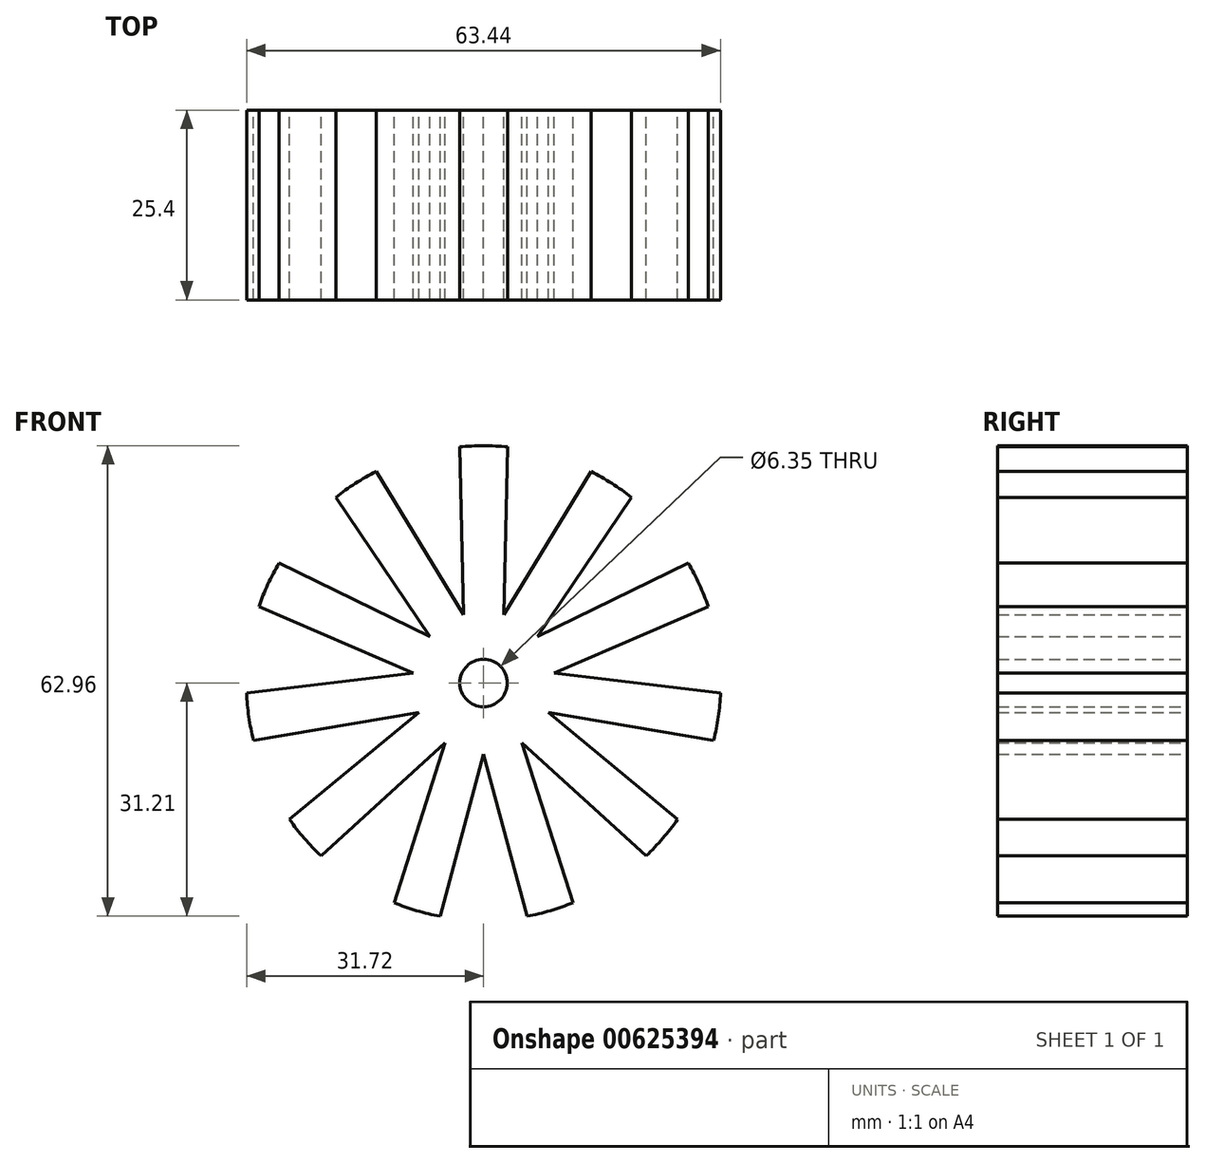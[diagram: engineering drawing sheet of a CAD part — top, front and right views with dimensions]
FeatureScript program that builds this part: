
annotation { "Feature Type Name" : "Feature", "Feature Type Description" : "" }
export const myFeature = defineFeature(function(context is Context, id is Id, definition is map)
    precondition{}
    {
        {
            var Q0;
            Q0=qCreatedBy(makeId("Front.planeOp"),FACE);
            var sketch = newSketch(context, id + "F0", { "sketchPlane" : qUnion([Q0])});
            skCircle(sketch, "E0", {"center": v(0, 0) * mm, "radius": 31.75 * mm});
            skLineSegment(sketch, "E1", {"start": v(-5.81, -31.21) * mm, "end": v(0, -9.52) * mm});
            skLineSegment(sketch, "E2", {"start": v(0, -9.53) * mm, "end": v(5.81, -31.21) * mm});
            skLineSegment(sketch, "E3", {"start": v(0, -31.75) * mm, "end": v(0, 0) * mm});
            skLineSegment(sketch, "E4.1.0", {"start": v(5.15, -8.01) * mm, "end": v(21.76, -23.12) * mm});
            skLineSegment(sketch, "E4.1.1", {"start": v(11.99, -29.4) * mm, "end": v(5.15, -8.01) * mm});
            skLineSegment(sketch, "E4.2.0", {"start": v(8.66, -3.96) * mm, "end": v(30.8, -7.68) * mm});
            skLineSegment(sketch, "E4.2.1", {"start": v(25.98, -18.25) * mm, "end": v(8.66, -3.96) * mm});
            skLineSegment(sketch, "E4.3.0", {"start": v(9.43, 1.36) * mm, "end": v(30.07, 10.2) * mm});
            skLineSegment(sketch, "E4.3.1", {"start": v(31.72, -1.31) * mm, "end": v(9.43, 1.36) * mm});
            skLineSegment(sketch, "E4.4.0", {"start": v(7.2, 6.24) * mm, "end": v(19.78, 24.83) * mm});
            skLineSegment(sketch, "E4.4.1", {"start": v(27.4, 16.05) * mm, "end": v(7.2, 6.24) * mm});
            skLineSegment(sketch, "E4.5.0", {"start": v(2.68, 9.14) * mm, "end": v(3.22, 31.59) * mm});
            skLineSegment(sketch, "E4.5.1", {"start": v(14.37, 28.31) * mm, "end": v(2.68, 9.14) * mm});
            skLineSegment(sketch, "E4.6.0", {"start": v(-2.68, 9.14) * mm, "end": v(-14.37, 28.31) * mm});
            skLineSegment(sketch, "E4.6.1", {"start": v(-3.22, 31.59) * mm, "end": v(-2.68, 9.14) * mm});
            skLineSegment(sketch, "E4.7.0", {"start": v(-7.2, 6.24) * mm, "end": v(-27.4, 16.05) * mm});
            skLineSegment(sketch, "E4.7.1", {"start": v(-19.78, 24.83) * mm, "end": v(-7.2, 6.24) * mm});
            skLineSegment(sketch, "E4.8.0", {"start": v(-9.43, 1.36) * mm, "end": v(-31.72, -1.31) * mm});
            skLineSegment(sketch, "E4.8.1", {"start": v(-30.07, 10.2) * mm, "end": v(-9.43, 1.36) * mm});
            skLineSegment(sketch, "E4.9.0", {"start": v(-8.66, -3.96) * mm, "end": v(-25.98, -18.25) * mm});
            skLineSegment(sketch, "E4.9.1", {"start": v(-30.8, -7.68) * mm, "end": v(-8.66, -3.96) * mm});
            skLineSegment(sketch, "E5.0.10.0", {"start": v(-5.15, -8.01) * mm, "end": v(-11.99, -29.4) * mm});
            skLineSegment(sketch, "E5.3.10.0", {"start": v(-21.76, -23.12) * mm, "end": v(-5.15, -8.01) * mm});
            skCircle(sketch, "E6", {"center": v(0, 0) * mm, "radius": 9.53 * mm});
            skLineSegment(sketch, "E7.bottom", {"start": v(3.18, 3.18) * mm, "end": v(-3.18, 3.18) * mm, "construction": true});
            skLineSegment(sketch, "E7.top", {"start": v(3.18, -3.18) * mm, "end": v(-3.17, -3.18) * mm, "construction": true});
            skLineSegment(sketch, "E7.left", {"start": v(3.18, 3.18) * mm, "end": v(3.18, -3.18) * mm, "construction": true});
            skLineSegment(sketch, "E7.right", {"start": v(-3.18, 3.17) * mm, "end": v(-3.18, -3.18) * mm, "construction": true});
            skCircle(sketch, "E8", {"center": v(0, 0) * mm, "radius": 3.17 * mm});
            skSolve(sketch);
        }
        {
            var Q0;
            {var subQ0=sQuery(id+"F0.wireOp",EDGE,"E4.7.0");Q0=makeQuery(id+"F0.imprint","IMPRINT",FACE,{"disambiguationData":[TD([[makeQuery(id+"F0.imprint","IMPRINT",EDGE,{"derivedFrom":subQ0}),1.0]])]});}
            var Q1;
            {var subQ0=sQuery(id+"F0.wireOp",EDGE,"E4.6.0");Q1=makeQuery(id+"F0.imprint","IMPRINT",FACE,{"disambiguationData":[TD([[makeQuery(id+"F0.imprint","IMPRINT",EDGE,{"derivedFrom":subQ0}),1.0]])]});}
            var Q2;
            {var subQ0=sQuery(id+"F0.wireOp",EDGE,"E6");var subQ8=makeQuery(id+"F0.imprint","INTERSECT",VERTEX,{"derivedFrom":[sQuery(id+"F0.wireOp",EDGE,"E4.3.0"),sQuery(id+"F0.wireOp",EDGE,"E4.3.1"),subQ0]});Q2=makeQuery(id+"F0.imprint","IMPRINT",FACE,{"disambiguationData":[TD([[makeQuery(id+"F0.imprint","IMPRINT",EDGE,{"disambiguationData":[TD([[subQ8,-1.0]])],"derivedFrom":subQ0}),1.0]])]});}
            var Q3;
            {var subQ0=sQuery(id+"F0.wireOp",EDGE,"E4.5.0");Q3=makeQuery(id+"F0.imprint","IMPRINT",FACE,{"disambiguationData":[TD([[makeQuery(id+"F0.imprint","IMPRINT",EDGE,{"derivedFrom":subQ0}),1.0]])]});}
            var Q4;
            {var subQ0=sQuery(id+"F0.wireOp",EDGE,"E4.4.0");Q4=makeQuery(id+"F0.imprint","IMPRINT",FACE,{"disambiguationData":[TD([[makeQuery(id+"F0.imprint","IMPRINT",EDGE,{"derivedFrom":subQ0}),1.0]])]});}
            var Q5;
            {var subQ0=sQuery(id+"F0.wireOp",EDGE,"E4.3.0");Q5=makeQuery(id+"F0.imprint","IMPRINT",FACE,{"disambiguationData":[TD([[makeQuery(id+"F0.imprint","IMPRINT",EDGE,{"derivedFrom":subQ0}),1.0]])]});}
            var Q6;
            {var subQ0=sQuery(id+"F0.wireOp",EDGE,"E4.2.0");Q6=makeQuery(id+"F0.imprint","IMPRINT",FACE,{"disambiguationData":[TD([[makeQuery(id+"F0.imprint","IMPRINT",EDGE,{"derivedFrom":subQ0}),1.0]])]});}
            var Q7;
            {var subQ0=sQuery(id+"F0.wireOp",EDGE,"E4.1.0");Q7=makeQuery(id+"F0.imprint","IMPRINT",FACE,{"disambiguationData":[TD([[makeQuery(id+"F0.imprint","IMPRINT",EDGE,{"derivedFrom":subQ0}),1.0]])]});}
            var Q8;
            {var subQ0=sQuery(id+"F0.wireOp",EDGE,"E2");Q8=makeQuery(id+"F0.imprint","IMPRINT",FACE,{"disambiguationData":[TD([[makeQuery(id+"F0.imprint","IMPRINT",EDGE,{"derivedFrom":subQ0}),1.0]])]});}
            var Q9;
            {var subQ0=sQuery(id+"F0.wireOp",EDGE,"E1");Q9=makeQuery(id+"F0.imprint","IMPRINT",FACE,{"disambiguationData":[TD([[makeQuery(id+"F0.imprint","IMPRINT",EDGE,{"derivedFrom":subQ0}),1.0]])]});}
            var Q10;
            {var subQ0=sQuery(id+"F0.wireOp",EDGE,"E4.9.0");Q10=makeQuery(id+"F0.imprint","IMPRINT",FACE,{"disambiguationData":[TD([[makeQuery(id+"F0.imprint","IMPRINT",EDGE,{"derivedFrom":subQ0}),1.0]])]});}
            var Q11;
            {var subQ0=sQuery(id+"F0.wireOp",EDGE,"E4.8.0");Q11=makeQuery(id+"F0.imprint","IMPRINT",FACE,{"disambiguationData":[TD([[makeQuery(id+"F0.imprint","IMPRINT",EDGE,{"derivedFrom":subQ0}),1.0]])]});}
            extrude(context, id + "F1", {"entities" : qUnion([Q0, Q1, Q2, Q3, Q4, Q5, Q6, Q7, Q8, Q9, Q10, Q11]), "depth" : 25.4 * mm, "offsetDistance" : 25.4 * mm});
        }
    });
